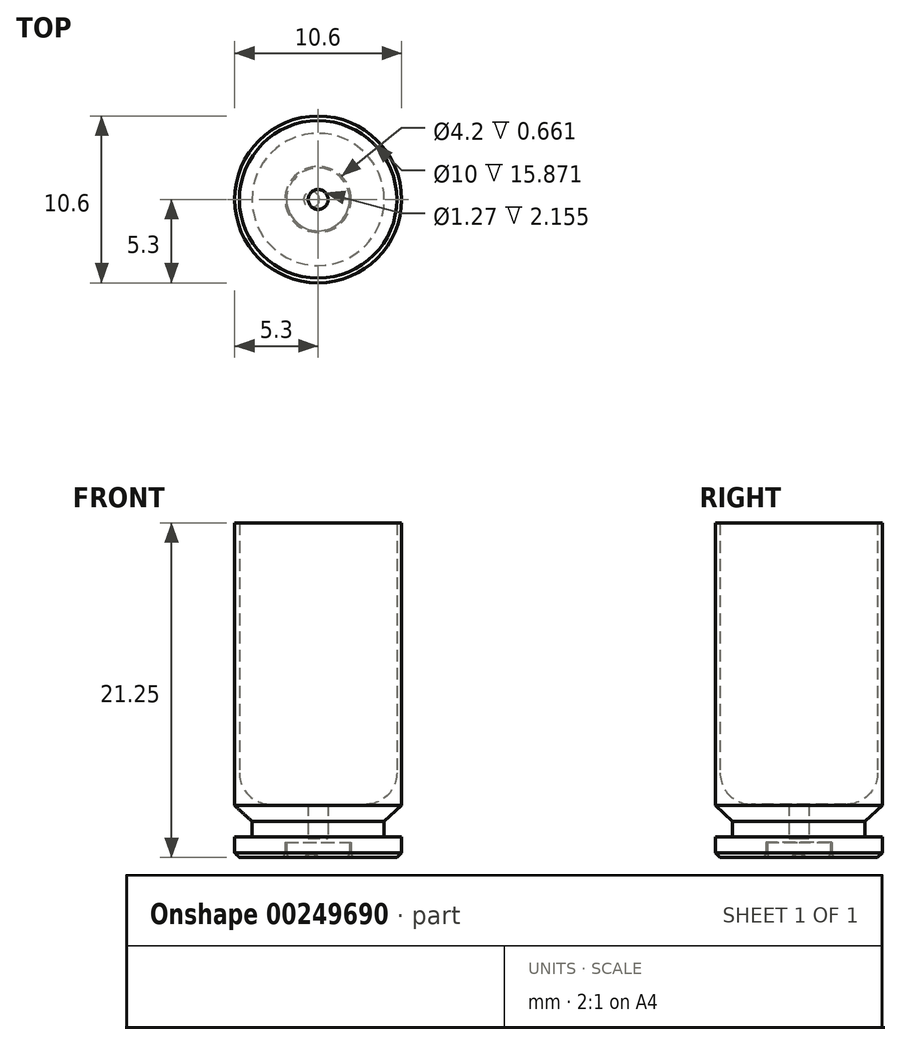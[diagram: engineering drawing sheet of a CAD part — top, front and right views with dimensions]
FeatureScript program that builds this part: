
annotation { "Feature Type Name" : "Feature", "Feature Type Description" : "" }
export const myFeature = defineFeature(function(context is Context, id is Id, definition is map)
    precondition{}
    {
        {
            var Q0;
            Q0=qCreatedBy(makeId("Front.planeOp"),FACE);
            var sketch = newSketch(context, id + "F0", { "sketchPlane" : qUnion([Q0])});
            skLineSegment(sketch, "E0", {"start": v(0, 0) * mm, "end": v(0, 21.25) * mm, "construction": true});
            skLineSegment(sketch, "E1", {"start": v(0, 0) * mm, "end": v(5.3, 0) * mm, "construction": true});
            skLineSegment(sketch, "E2", {"start": v(5.3, 0) * mm, "end": v(5.3, 1.3) * mm});
            skLineSegment(sketch, "E3", {"start": v(5.3, 1.3) * mm, "end": v(4.2, 1.3) * mm});
            skLineSegment(sketch, "E4", {"start": v(4.2, 1.3) * mm, "end": v(4.2, 2.3) * mm});
            skLineSegment(sketch, "E5", {"start": v(4.2, 2.3) * mm, "end": v(5.3, 3.3) * mm});
            skLineSegment(sketch, "E6", {"start": v(5.3, 3.3) * mm, "end": v(5.3, 21.25) * mm});
            skLineSegment(sketch, "E7", {"start": v(5.3, 21.25) * mm, "end": v(0, 21.25) * mm, "construction": true});
            skLineSegment(sketch, "E8.0", {"start": v(5, 3.38) * mm, "end": v(5, 21.25) * mm});
            skLineSegment(sketch, "E9", {"start": v(2.1, 0) * mm, "end": v(2.1, 0.96) * mm});
            skLineSegment(sketch, "E10", {"start": v(2.1, 0.96) * mm, "end": v(2, 0.96) * mm});
            skLineSegment(sketch, "E11", {"start": v(2, 0.96) * mm, "end": v(2, 0) * mm});
            skLineSegment(sketch, "E12", {"start": v(2, 0) * mm, "end": v(0, 0) * mm});
            skLineSegment(sketch, "E13", {"start": v(2.1, 0) * mm, "end": v(5.3, 0) * mm});
            skLineSegment(sketch, "E14", {"start": v(0, 1.22) * mm, "end": v(0.63, 1.22) * mm});
            skLineSegment(sketch, "E15", {"start": v(0.63, 1.22) * mm, "end": v(0.63, 3.38) * mm});
            skLineSegment(sketch, "E16", {"start": v(0.63, 3.38) * mm, "end": v(5, 3.38) * mm});
            skLineSegment(sketch, "E17", {"start": v(0, 1.22) * mm, "end": v(0, 0) * mm});
            skLineSegment(sketch, "E18", {"start": v(5, 21.25) * mm, "end": v(5.3, 21.25) * mm});
            skSolve(sketch);
        }
        {
            var Q0;
            Q0 = qSketchRegion(id + "F0", true);
            var Q1;
            Q1=sQuery(id+"F0.wireOp",EDGE,"E0");
            revolve(context, id + "F1", {"entities" : qUnion([Q0]), "axis" : qUnion([Q1]), "revolveType" : RevolveType.FULL});
        }
        {
            var Q0;
            Q0=makeQuery(id+"F1.opRevolve","SWEPT_EDGE",EDGE,{"disambiguationData":[OSD([sQuery(id+"F0.wireOp",EDGE,"E8.0"),sQuery(id+"F0.wireOp",EDGE,"E16")])]});
            fillet(context, id + "F2", {"entities" : qUnion([Q0]), "radius" : 2 * mm, "tangentPropagation" : true, "allowEdgeOverflow" : false});
        }
        {
            var Q0;
            Q0=makeQuery(id+"F1.opRevolve","SWEPT_EDGE",EDGE,{"disambiguationData":[OSD([sQuery(id+"F0.wireOp",EDGE,"E9"),sQuery(id+"F0.wireOp",EDGE,"E13")])]});
            var Q1;
            Q1=makeQuery(id+"F1.opRevolve","SWEPT_EDGE",EDGE,{"disambiguationData":[OSD([sQuery(id+"F0.wireOp",EDGE,"E11"),sQuery(id+"F0.wireOp",EDGE,"E12")])]});
            fillet(context, id + "F3", {"entities" : qUnion([Q0, Q1]), "radius" : .3 * mm, "tangentPropagation" : true, "allowEdgeOverflow" : false});
        }
        {
            var Q0;
            Q0=makeQuery(id+"F1.opRevolve","SWEPT_EDGE",EDGE,{"disambiguationData":[OSD([sQuery(id+"F0.wireOp",EDGE,"E2"),sQuery(id+"F0.wireOp",EDGE,"E13")])]});
            chamfer(context, id + "F4", {"entities" : qUnion([Q0]), "width" : .3 * mm, "tangentPropagation" : true});
        }
        {
            var Q0;
            Q0=qCreatedBy(makeId("Front.planeOp"),FACE);
            var sketch = newSketch(context, id + "F5", { "sketchPlane" : qUnion([Q0])});
            skLineSegment(sketch, "E19", {"start": v(-0.42, 0) * mm, "end": v(-0.42, 0.2) * mm});
            skLineSegment(sketch, "E20", {"start": v(-0.42, 0) * mm, "end": v(-0.92, 0) * mm});
            skArc(sketch, "E21", {"start": v(-0.42, 0.2) * mm, "mid": v(-0.69, 0.15) * mm, "end": v(-0.92, 0) * mm});
            skLineSegment(sketch, "E22", {"start": v(-0.42, 0.2) * mm, "end": v(0.33, 0.2) * mm, "construction": true});
            skSolve(sketch);
        }
        {
            var Q0;
            Q0 = qSketchRegion(id + "F5", true);
            var Q1;
            Q1=sQuery(id+"F5.wireOp",EDGE,"E19");
            revolve(context, id + "F6", {"operationType" : NewBodyOperationType.REMOVE, "entities" : qUnion([Q0]), "axis" : qUnion([Q1]), "revolveType" : RevolveType.FULL, "oppositeDirection" : true});
        }
    });
